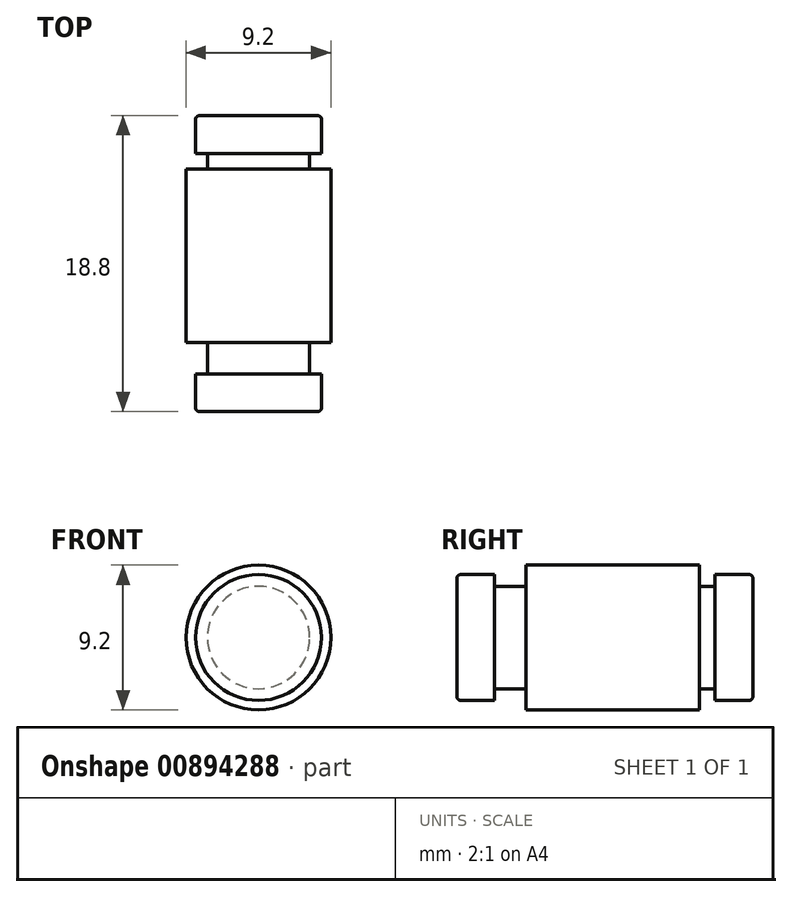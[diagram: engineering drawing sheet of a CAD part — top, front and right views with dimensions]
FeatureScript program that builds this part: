
annotation { "Feature Type Name" : "Feature", "Feature Type Description" : "" }
export const myFeature = defineFeature(function(context is Context, id is Id, definition is map)
    precondition{}
    {
        {
            var Q0;
            Q0=qCreatedBy(makeId("Right.planeOp"),FACE);
            var sketch = newSketch(context, id + "F0", { "sketchPlane" : qUnion([Q0])});
            skLineSegment(sketch, "E0.bottom", {"start": v(0, 0) * mm, "end": v(18.8, 0) * mm});
            skLineSegment(sketch, "E0.top", {"start": v(0.25, 4) * mm, "end": v(2.4, 4) * mm});
            skLineSegment(sketch, "E1", {"start": v(0, 0) * mm, "end": v(0, 3.75) * mm});
            skLineSegment(sketch, "E2", {"start": v(2.4, 4) * mm, "end": v(2.4, 3.25) * mm});
            skLineSegment(sketch, "E3", {"start": v(2.4, 3.25) * mm, "end": v(4.4, 3.25) * mm});
            skLineSegment(sketch, "E4", {"start": v(4.4, 3.25) * mm, "end": v(4.4, 4.6) * mm});
            skLineSegment(sketch, "E5", {"start": v(4.4, 4.6) * mm, "end": v(15.4, 4.6) * mm});
            skLineSegment(sketch, "E6", {"start": v(15.4, 4.6) * mm, "end": v(15.4, 3.25) * mm});
            skLineSegment(sketch, "E7", {"start": v(15.4, 3.25) * mm, "end": v(16.4, 3.25) * mm});
            skLineSegment(sketch, "E8", {"start": v(16.4, 3.25) * mm, "end": v(16.4, 4) * mm});
            skLineSegment(sketch, "E9", {"start": v(16.4, 4) * mm, "end": v(18.55, 4) * mm});
            skLineSegment(sketch, "E10", {"start": v(18.8, 3.75) * mm, "end": v(18.8, 0) * mm});
            skPoint(sketch, "E11.visualSharp", {"position": v(18.8, 4) * mm});
            skArc(sketch, "E11.filletArc", {"start": v(18.8, 3.75) * mm, "mid": v(18.73, 3.93) * mm, "end": v(18.55, 4) * mm});
            skPoint(sketch, "E12.visualSharp", {"position": v(0, 4) * mm});
            skArc(sketch, "E12.filletArc", {"start": v(0.25, 4) * mm, "mid": v(0.07, 3.93) * mm, "end": v(0, 3.75) * mm});
            skSolve(sketch);
        }
        {
            var Q0;
            Q0=makeQuery(id+"F0.imprint","IMPRINT",FACE,{"disambiguationData":[TD([[makeQuery(id+"F0.imprint","IMPRINT",EDGE,{"derivedFrom":sQuery(id+"F0.wireOp",EDGE,"E0.bottom")}),1.0]])]});
            var Q1;
            Q1=sQuery(id+"F0.wireOp",EDGE,"E0.bottom");
            revolve(context, id + "F1", {"surfaceOperationType" : NewSurfaceOperationType.NEW, "entities" : qUnion([Q0]), "axis" : qUnion([Q1]), "revolveType" : RevolveType.FULL});
        }
    });
